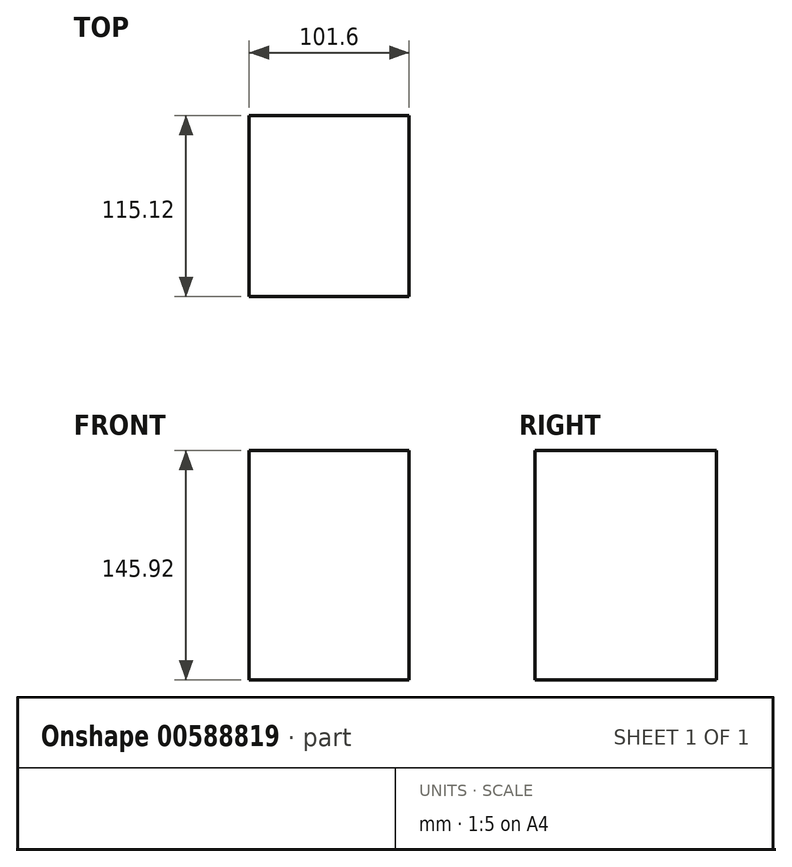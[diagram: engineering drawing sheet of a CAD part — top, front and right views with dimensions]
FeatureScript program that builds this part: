
annotation { "Feature Type Name" : "Feature", "Feature Type Description" : "" }
export const myFeature = defineFeature(function(context is Context, id is Id, definition is map)
    precondition{}
    {
        {
            var Q0;
            Q0=qCreatedBy(makeId("Right.planeOp"),FACE);
            var sketch = newSketch(context, id + "F0", { "sketchPlane" : qUnion([Q0])});
            skLineSegment(sketch, "E0.bottom", {"start": v(-58.57, 73.25) * mm, "end": v(56.55, 73.25) * mm});
            skLineSegment(sketch, "E0.top", {"start": v(-58.57, -72.67) * mm, "end": v(56.55, -72.67) * mm});
            skLineSegment(sketch, "E0.left", {"start": v(-58.57, 73.25) * mm, "end": v(-58.57, -72.67) * mm});
            skLineSegment(sketch, "E0.right", {"start": v(56.55, 73.25) * mm, "end": v(56.55, -72.67) * mm});
            skSolve(sketch);
        }
        {
            var Q0;
            Q0=makeQuery(id+"F0.imprint","IMPRINT",FACE,{"disambiguationData":[TD([[makeQuery(id+"F0.imprint","IMPRINT",EDGE,{"derivedFrom":sQuery(id+"F0.wireOp",EDGE,"E0.bottom")}),-1.0]])]});
            var Q1;
            Q1=sQuery(id+"F0.wireOp",EDGE,"E0.left");
            var Q2;
            Q2=sQuery(id+"F0.wireOp",EDGE,"E0.right");
            var Q3;
            Q3=sQuery(id+"F0.wireOp",EDGE,"E0.bottom");
            var Q4;
            Q4=sQuery(id+"F0.wireOp",EDGE,"E0.top");
            extrude(context, id + "F1", {"entities" : qUnion([Q0]), "bodyType" : ToolBodyType.SURFACE, "surfaceEntities" : qUnion([Q1, Q2, Q3, Q4]), "oppositeDirection" : true, "depth" : 101.6 * mm, "offsetDistance" : 25.4 * mm});
        }
    });
